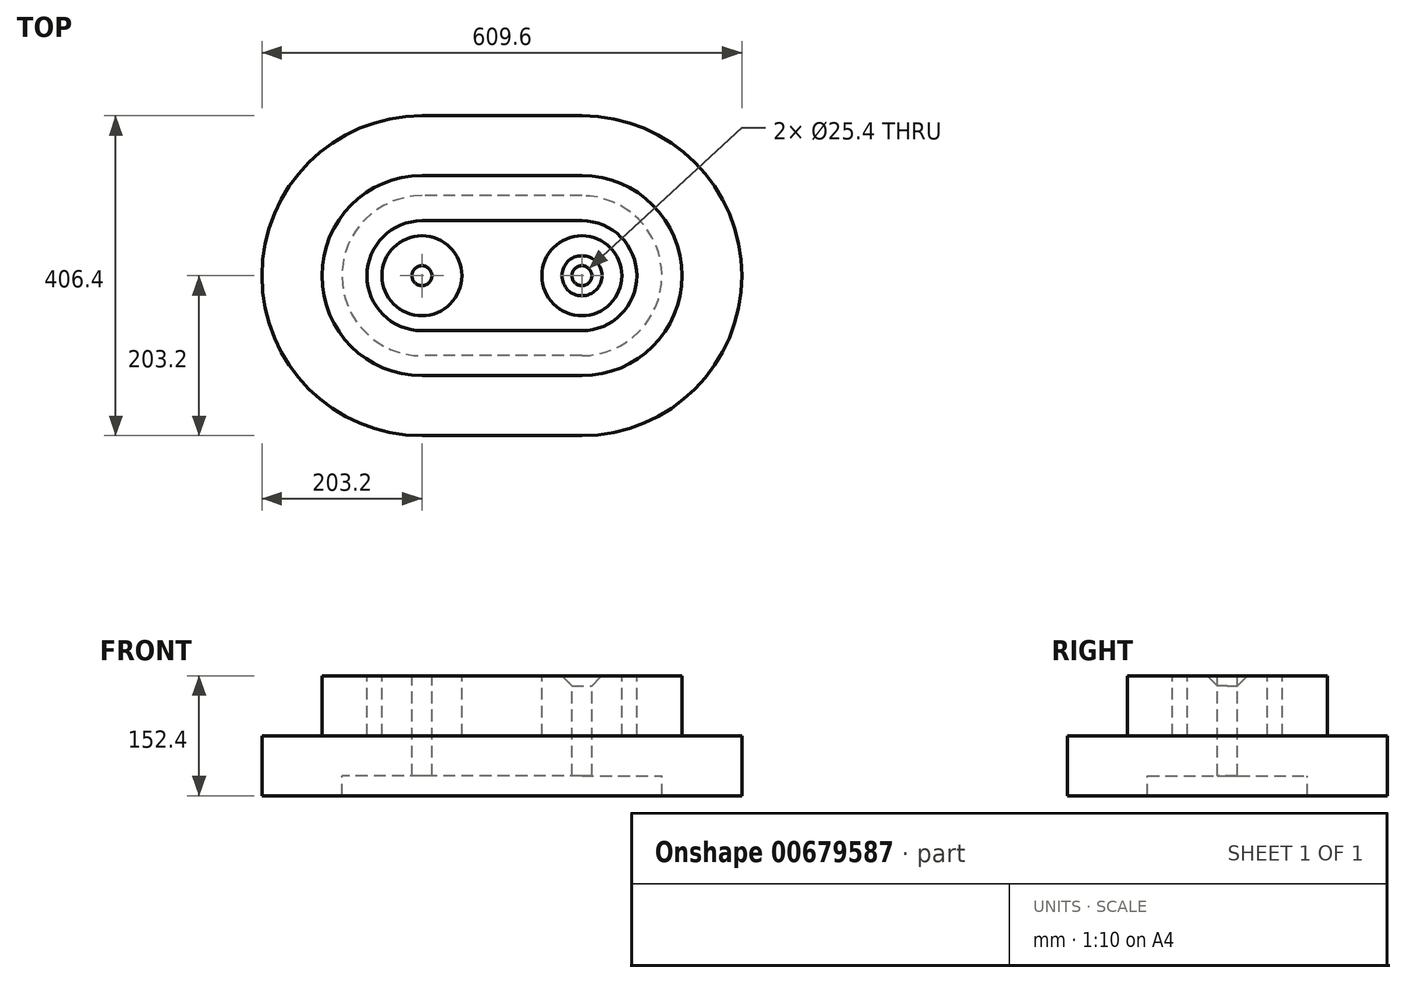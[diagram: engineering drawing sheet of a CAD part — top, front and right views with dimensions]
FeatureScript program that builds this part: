
annotation { "Feature Type Name" : "Feature", "Feature Type Description" : "" }
export const myFeature = defineFeature(function(context is Context, id is Id, definition is map)
    precondition{}
    {
        {
            var Q0;
            Q0=qCreatedBy(makeId("Top.planeOp"),FACE);
            var sketch = newSketch(context, id + "F0", { "sketchPlane" : qUnion([Q0])});
            skLineSegment(sketch, "E0.bottom", {"start": v(101.6, -203.2) * mm, "end": v(-101.6, -203.2) * mm});
            skLineSegment(sketch, "E0.top", {"start": v(101.6, 203.2) * mm, "end": v(-101.6, 203.2) * mm});
            skLineSegment(sketch, "E0.left", {"start": v(304.8, 0) * mm, "end": v(304.8, 0) * mm});
            skLineSegment(sketch, "E0.right", {"start": v(-304.8, 0) * mm, "end": v(-304.8, 0) * mm});
            skPoint(sketch, "E0.middle", {"position": v(0, 0) * mm});
            skPoint(sketch, "E1.visualSharp", {"position": v(-304.8, 203.2) * mm});
            skArc(sketch, "E1.filletArc", {"start": v(-101.6, 203.2) * mm, "mid": v(-245.28, 143.68) * mm, "end": v(-304.8, 0) * mm});
            skPoint(sketch, "E2.visualSharp", {"position": v(-304.8, -203.2) * mm});
            skArc(sketch, "E2.filletArc", {"start": v(-304.8, 0) * mm, "mid": v(-245.28, -143.68) * mm, "end": v(-101.6, -203.2) * mm});
            skPoint(sketch, "E3.visualSharp", {"position": v(304.8, -203.2) * mm});
            skArc(sketch, "E3.filletArc", {"start": v(101.6, -203.2) * mm, "mid": v(245.28, -143.68) * mm, "end": v(304.8, 0) * mm});
            skPoint(sketch, "E4.visualSharp", {"position": v(304.8, 203.2) * mm});
            skArc(sketch, "E4.filletArc", {"start": v(304.8, 0) * mm, "mid": v(245.28, 143.68) * mm, "end": v(101.6, 203.2) * mm});
            skLineSegment(sketch, "E5.bottom", {"start": v(101.6, -127) * mm, "end": v(-101.6, -127) * mm});
            skLineSegment(sketch, "E5.top", {"start": v(101.6, 127) * mm, "end": v(-101.6, 127) * mm});
            skLineSegment(sketch, "E5.left", {"start": v(228.6, 0) * mm, "end": v(228.6, 0) * mm});
            skLineSegment(sketch, "E5.right", {"start": v(-228.6, 0) * mm, "end": v(-228.6, 0) * mm});
            skPoint(sketch, "E6.visualSharp", {"position": v(-228.6, 127) * mm});
            skArc(sketch, "E7.filletArc", {"start": v(-101.6, 127) * mm, "mid": v(-191.4, 89.8) * mm, "end": v(-228.6, 0) * mm});
            skPoint(sketch, "E8.visualSharp", {"position": v(228.6, 127) * mm});
            skArc(sketch, "E8.filletArc", {"start": v(228.6, 0) * mm, "mid": v(191.4, 89.8) * mm, "end": v(101.6, 127) * mm});
            skPoint(sketch, "E9.visualSharp", {"position": v(228.6, -127) * mm});
            skArc(sketch, "E9.filletArc", {"start": v(101.6, -127) * mm, "mid": v(191.4, -89.8) * mm, "end": v(228.6, 0) * mm});
            skPoint(sketch, "E10.visualSharp", {"position": v(-228.6, -127) * mm});
            skArc(sketch, "E10.filletArc", {"start": v(-228.6, 0) * mm, "mid": v(-191.4, -89.8) * mm, "end": v(-101.6, -127) * mm});
            skCircle(sketch, "E11", {"center": v(101.6, 0) * mm, "radius": 25.4 * mm});
            skCircle(sketch, "E12.MirrorC", {"center": v(-101.6, 0) * mm, "radius": 25.4 * mm});
            skCircle(sketch, "E13", {"center": v(101.6, 0) * mm, "radius": 50.8 * mm});
            skCircle(sketch, "E14.MirrorC", {"center": v(-101.6, 0) * mm, "radius": 50.8 * mm});
            skCircle(sketch, "E15", {"center": v(101.6, 0) * mm, "radius": 12.7 * mm});
            skCircle(sketch, "E16.MirrorC", {"center": v(-101.6, 0) * mm, "radius": 12.7 * mm});
            skLineSegment(sketch, "E17.bottom", {"start": v(101.6, 69.85) * mm, "end": v(-101.6, 69.85) * mm});
            skLineSegment(sketch, "E17.top", {"start": v(101.6, -69.85) * mm, "end": v(-101.6, -69.85) * mm});
            skLineSegment(sketch, "E17.left", {"start": v(171.45, 0) * mm, "end": v(171.45, 0) * mm});
            skLineSegment(sketch, "E17.right", {"start": v(-171.45, 0) * mm, "end": v(-171.45, 0) * mm});
            skPoint(sketch, "E18.visualSharp", {"position": v(-171.45, 69.85) * mm});
            skArc(sketch, "E18.filletArc", {"start": v(-101.6, 69.85) * mm, "mid": v(-151, 49.4) * mm, "end": v(-171.45, 0) * mm});
            skPoint(sketch, "E19.visualSharp", {"position": v(171.45, 69.85) * mm});
            skArc(sketch, "E19.filletArc", {"start": v(171.45, 0) * mm, "mid": v(151, 49.4) * mm, "end": v(101.6, 69.85) * mm});
            skPoint(sketch, "E20.visualSharp", {"position": v(171.45, -69.85) * mm});
            skArc(sketch, "E20.filletArc", {"start": v(101.6, -69.85) * mm, "mid": v(151, -49.4) * mm, "end": v(171.45, 0) * mm});
            skPoint(sketch, "E21.visualSharp", {"position": v(-171.45, -69.85) * mm});
            skArc(sketch, "E21.filletArc", {"start": v(-171.45, 0) * mm, "mid": v(-151, -49.4) * mm, "end": v(-101.6, -69.85) * mm});
            skLineSegment(sketch, "E22.bottom", {"start": v(101.6, -101.6) * mm, "end": v(-101.6, -101.6) * mm});
            skLineSegment(sketch, "E22.top", {"start": v(101.6, 101.6) * mm, "end": v(-101.6, 101.6) * mm});
            skLineSegment(sketch, "E22.left", {"start": v(203.2, 0) * mm, "end": v(203.2, 0) * mm});
            skLineSegment(sketch, "E22.right", {"start": v(-203.2, 0) * mm, "end": v(-203.2, 0) * mm});
            skPoint(sketch, "E23.visualSharp", {"position": v(-203.2, 101.6) * mm});
            skArc(sketch, "E23.filletArc", {"start": v(-101.6, 101.6) * mm, "mid": v(-173.44, 71.84) * mm, "end": v(-203.2, 0) * mm});
            skPoint(sketch, "E24.visualSharp", {"position": v(203.2, 101.6) * mm});
            skArc(sketch, "E24.filletArc", {"start": v(203.2, 0) * mm, "mid": v(173.44, 71.84) * mm, "end": v(101.6, 101.6) * mm});
            skPoint(sketch, "E25.visualSharp", {"position": v(203.2, -101.6) * mm});
            skArc(sketch, "E25.filletArc", {"start": v(101.6, -101.6) * mm, "mid": v(173.44, -71.84) * mm, "end": v(203.2, 0) * mm});
            skPoint(sketch, "E26.visualSharp", {"position": v(-203.2, -101.6) * mm});
            skArc(sketch, "E26.filletArc", {"start": v(-203.2, 0) * mm, "mid": v(-173.44, -71.84) * mm, "end": v(-101.6, -101.6) * mm});
            skSolve(sketch);
        }
        {
            var Q0;
            Q0=makeQuery(id+"F0.imprint","IMPRINT",FACE,{"disambiguationData":[TD([[makeQuery(id+"F0.imprint","IMPRINT",EDGE,{"derivedFrom":sQuery(id+"F0.wireOp",EDGE,"E13")}),-1.0]])]});
            var Q1;
            Q1=makeQuery(id+"F0.imprint","IMPRINT",FACE,{"disambiguationData":[TD([[makeQuery(id+"F0.imprint","IMPRINT",EDGE,{"derivedFrom":sQuery(id+"F0.wireOp",EDGE,"E12.MirrorC")}),-1.0]])]});
            var Q2;
            Q2=makeQuery(id+"F0.imprint","IMPRINT",FACE,{"disambiguationData":[TD([[makeQuery(id+"F0.imprint","IMPRINT",EDGE,{"derivedFrom":sQuery(id+"F0.wireOp",EDGE,"E12.MirrorC")}),1.0]])]});
            var Q3;
            Q3=makeQuery(id+"F0.imprint","IMPRINT",FACE,{"disambiguationData":[TD([[makeQuery(id+"F0.imprint","IMPRINT",EDGE,{"derivedFrom":sQuery(id+"F0.wireOp",EDGE,"E5.bottom")}),-1.0]])]});
            var Q4;
            Q4=makeQuery(id+"F0.imprint","IMPRINT",FACE,{"disambiguationData":[TD([[makeQuery(id+"F0.imprint","IMPRINT",EDGE,{"derivedFrom":sQuery(id+"F0.wireOp",EDGE,"E17.bottom")}),-1.0]])]});
            var Q5;
            Q5=makeQuery(id+"F0.imprint","IMPRINT",FACE,{"disambiguationData":[TD([[makeQuery(id+"F0.imprint","IMPRINT",EDGE,{"derivedFrom":sQuery(id+"F0.wireOp",EDGE,"E11")}),1.0]])]});
            var Q6;
            Q6=makeQuery(id+"F0.imprint","IMPRINT",FACE,{"disambiguationData":[TD([[makeQuery(id+"F0.imprint","IMPRINT",EDGE,{"derivedFrom":sQuery(id+"F0.wireOp",EDGE,"E11")}),-1.0]])]});
            extrude(context, id + "F1", {"entities" : qUnion([Q0, Q1, Q2, Q3, Q4, Q5, Q6]), "oppositeDirection" : true, "depth" : 76.2 * mm, "offsetDistance" : 25.4 * mm});
        }
        {
            var Q0;
            Q0=makeQuery(id+"F0.imprint","IMPRINT",FACE,{"disambiguationData":[TD([[makeQuery(id+"F0.imprint","IMPRINT",EDGE,{"derivedFrom":sQuery(id+"F0.wireOp",EDGE,"E0.bottom")}),-1.0]])]});
            var Q1;
            Q1=makeQuery(id+"F0.imprint","IMPRINT",FACE,{"disambiguationData":[TD([[makeQuery(id+"F0.imprint","IMPRINT",EDGE,{"derivedFrom":sQuery(id+"F0.wireOp",EDGE,"E5.bottom")}),-1.0]])]});
            var Q2;
            Q2=makeQuery(id+"F0.imprint","IMPRINT",FACE,{"disambiguationData":[TD([[makeQuery(id+"F0.imprint","IMPRINT",EDGE,{"derivedFrom":sQuery(id+"F0.wireOp",EDGE,"E17.bottom")}),-1.0]])]});
            var Q3;
            Q3=makeQuery(id+"F0.imprint","IMPRINT",FACE,{"disambiguationData":[TD([[makeQuery(id+"F0.imprint","IMPRINT",EDGE,{"derivedFrom":sQuery(id+"F0.wireOp",EDGE,"E13")}),-1.0]])]});
            var Q4;
            Q4=makeQuery(id+"F0.imprint","IMPRINT",FACE,{"disambiguationData":[TD([[makeQuery(id+"F0.imprint","IMPRINT",EDGE,{"derivedFrom":sQuery(id+"F0.wireOp",EDGE,"E12.MirrorC")}),1.0]])]});
            var Q5;
            Q5=makeQuery(id+"F0.imprint","IMPRINT",FACE,{"disambiguationData":[TD([[makeQuery(id+"F0.imprint","IMPRINT",EDGE,{"derivedFrom":sQuery(id+"F0.wireOp",EDGE,"E12.MirrorC")}),-1.0]])]});
            var Q6;
            Q6=makeQuery(id+"F0.imprint","IMPRINT",FACE,{"disambiguationData":[TD([[makeQuery(id+"F0.imprint","IMPRINT",EDGE,{"derivedFrom":sQuery(id+"F0.wireOp",EDGE,"E11")}),-1.0]])]});
            var Q7;
            Q7=makeQuery(id+"F0.imprint","IMPRINT",FACE,{"disambiguationData":[TD([[makeQuery(id+"F0.imprint","IMPRINT",EDGE,{"derivedFrom":sQuery(id+"F0.wireOp",EDGE,"E11")}),1.0]])]});
            extrude(context, id + "F2", {"entities" : qUnion([Q0, Q1, Q2, Q3, Q4, Q5, Q6, Q7]), "operationType" : NewBodyOperationType.ADD, "oppositeDirection" : true, "depth" : 152.4 * mm, "offsetDistance" : 25.4 * mm, "hasSecondDirection" : true, "secondDirectionOppositeDirection" : true, "secondDirectionDepth" : 76.2 * mm});
        }
        {
            var Q0;
            Q0=makeQuery(id+"F0.imprint","IMPRINT",FACE,{"disambiguationData":[TD([[makeQuery(id+"F0.imprint","IMPRINT",EDGE,{"derivedFrom":sQuery(id+"F0.wireOp",EDGE,"E17.bottom")}),-1.0]])]});
            var Q1;
            Q1=makeQuery(id+"F0.imprint","IMPRINT",FACE,{"disambiguationData":[TD([[makeQuery(id+"F0.imprint","IMPRINT",EDGE,{"derivedFrom":sQuery(id+"F0.wireOp",EDGE,"E13")}),-1.0]])]});
            var Q2;
            Q2=makeQuery(id+"F0.imprint","IMPRINT",FACE,{"disambiguationData":[TD([[makeQuery(id+"F0.imprint","IMPRINT",EDGE,{"derivedFrom":sQuery(id+"F0.wireOp",EDGE,"E11")}),-1.0]])]});
            var Q3;
            Q3=makeQuery(id+"F0.imprint","IMPRINT",FACE,{"disambiguationData":[TD([[makeQuery(id+"F0.imprint","IMPRINT",EDGE,{"derivedFrom":sQuery(id+"F0.wireOp",EDGE,"E11")}),1.0]])]});
            var Q4;
            Q4=makeQuery(id+"F0.imprint","IMPRINT",FACE,{"disambiguationData":[TD([[makeQuery(id+"F0.imprint","IMPRINT",EDGE,{"derivedFrom":sQuery(id+"F0.wireOp",EDGE,"E12.MirrorC")}),1.0]])]});
            var Q5;
            Q5=makeQuery(id+"F0.imprint","IMPRINT",FACE,{"disambiguationData":[TD([[makeQuery(id+"F0.imprint","IMPRINT",EDGE,{"derivedFrom":sQuery(id+"F0.wireOp",EDGE,"E12.MirrorC")}),-1.0]])]});
            var Q6;
            Q6=makeQuery(id+"F0.imprint","IMPRINT",FACE,{"disambiguationData":[TD([[makeQuery(id+"F0.imprint","IMPRINT",EDGE,{"derivedFrom":sQuery(id+"F0.wireOp",EDGE,"E16.MirrorC")}),-1.0]])]});
            var Q7;
            Q7=makeQuery(id+"F0.imprint","IMPRINT",FACE,{"disambiguationData":[TD([[makeQuery(id+"F0.imprint","IMPRINT",EDGE,{"derivedFrom":sQuery(id+"F0.wireOp",EDGE,"E15")}),1.0]])]});
            extrude(context, id + "F3", {"entities" : qUnion([Q0, Q1, Q2, Q3, Q4, Q5, Q6, Q7]), "operationType" : NewBodyOperationType.REMOVE, "oppositeDirection" : true, "depth" : 152.4 * mm, "offsetDistance" : 25.4 * mm, "hasSecondDirection" : true, "secondDirectionOppositeDirection" : true, "secondDirectionDepth" : 127 * mm});
        }
        {
            var Q0;
            Q0=makeQuery(id+"F0.imprint","IMPRINT",FACE,{"disambiguationData":[TD([[makeQuery(id+"F0.imprint","IMPRINT",EDGE,{"derivedFrom":sQuery(id+"F0.wireOp",EDGE,"E13")}),-1.0]])]});
            extrude(context, id + "F4", {"entities" : qUnion([Q0]), "operationType" : NewBodyOperationType.REMOVE, "oppositeDirection" : true, "depth" : 76.2 * mm, "offsetDistance" : 25.4 * mm});
        }
        {
            var Q0;
            Q0=qCreatedBy(makeId("Front.planeOp"),FACE);
            var sketch = newSketch(context, id + "F5", { "sketchPlane" : qUnion([Q0])});
            skLineSegment(sketch, "E27", {"start": v(0, 0) * mm, "end": v(76.2, 0) * mm});
            skLineSegment(sketch, "E28", {"start": v(76.2, 0) * mm, "end": v(101.6, 0) * mm});
            skLineSegment(sketch, "E29", {"start": v(101.6, 0) * mm, "end": v(127, 0) * mm});
            skLineSegment(sketch, "E30", {"start": v(101.6, 0) * mm, "end": v(101.6, -12.7) * mm});
            skLineSegment(sketch, "E31", {"start": v(101.6, -12.7) * mm, "end": v(114.3, -12.7) * mm});
            skLineSegment(sketch, "E32", {"start": v(114.3, -12.7) * mm, "end": v(127, 0) * mm});
            skSolve(sketch);
        }
        {
            var Q0;
            Q0=makeQuery(id+"F5.imprint","IMPRINT",FACE,{"disambiguationData":[TD([[makeQuery(id+"F5.imprint","IMPRINT",EDGE,{"derivedFrom":sQuery(id+"F5.wireOp",EDGE,"E29")}),-1.0]])]});
            var Q1;
            Q1=sQuery(id+"F5.wireOp",EDGE,"E30");
            revolve(context, id + "F6", {"operationType" : NewBodyOperationType.REMOVE, "entities" : qUnion([Q0]), "axis" : qUnion([Q1]), "revolveType" : RevolveType.FULL, "oppositeDirection" : true});
        }
    });
